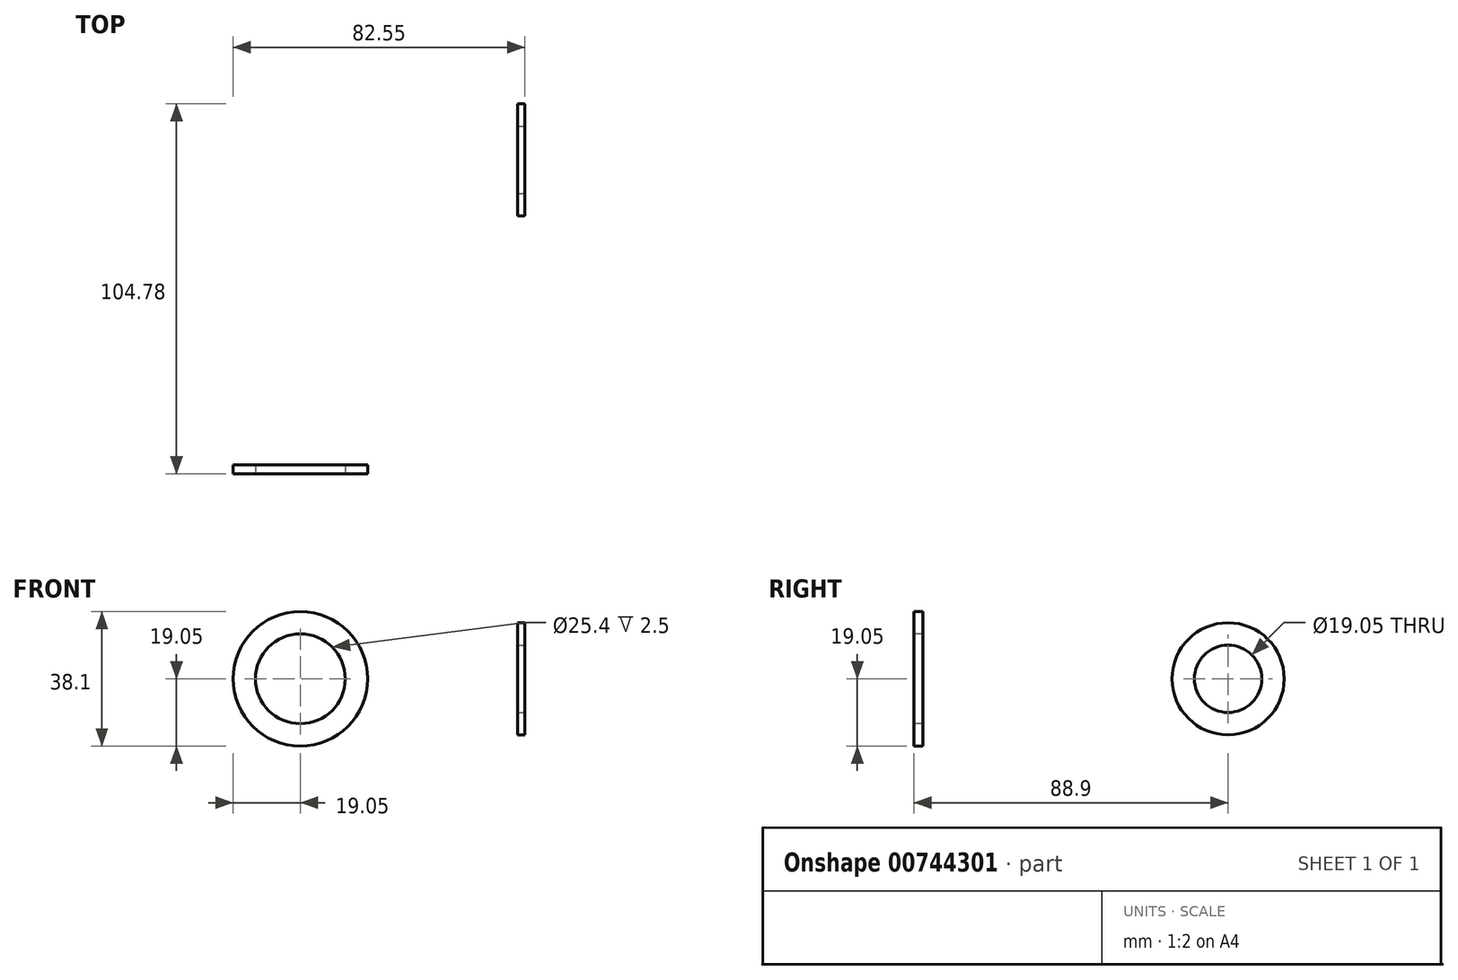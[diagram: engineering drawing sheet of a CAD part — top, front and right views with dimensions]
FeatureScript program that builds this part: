
annotation { "Feature Type Name" : "Feature", "Feature Type Description" : "" }
export const myFeature = defineFeature(function(context is Context, id is Id, definition is map)
    precondition{}
    {
        {
            var Q0;
            Q0=qCreatedBy(makeId("Front.planeOp"),FACE);
            var sketch = newSketch(context, id + "F0", { "sketchPlane" : qUnion([Q0])});
            skCircle(sketch, "E0", {"center": v(-63.5, 0) * mm, "radius": 19.05 * mm});
            skCircle(sketch, "E1", {"center": v(-63.5, 0) * mm, "radius": 12.7 * mm});
            skSolve(sketch);
        }
        {
            assignVariable(context, id + "F1", {"name" : "A", "anyValue" : 2.5});
        }
        {
            var Q0;
            Q0 = qSketchRegion(id + "F0", true);
            extrude(context, id + "F2", {"entities" : qUnion([Q0]), "oppositeDirection" : true, "depth" : (getVariable(context, 'A')) * mm, "offsetDistance" : 25.4 * mm});
        }
        {
            var Q0;
            Q0=qCreatedBy(makeId("Right.planeOp"),FACE);
            var sketch = newSketch(context, id + "F3", { "sketchPlane" : qUnion([Q0])});
            skCircle(sketch, "E2", {"center": v(88.9, 0) * mm, "radius": 15.88 * mm});
            skCircle(sketch, "E3", {"center": v(88.9, 0) * mm, "radius": 9.53 * mm});
            skSolve(sketch);
        }
        {
            assignVariable(context, id + "F4", {"name" : "B", "anyValue" : 2});
        }
        {
            var Q0;
            Q0 = qSketchRegion(id + "F3", true);
            extrude(context, id + "F5", {"entities" : qUnion([Q0]), "oppositeDirection" : true, "depth" : (getVariable(context, 'B')) * mm, "offsetDistance" : 25.4 * mm});
        }
    });
